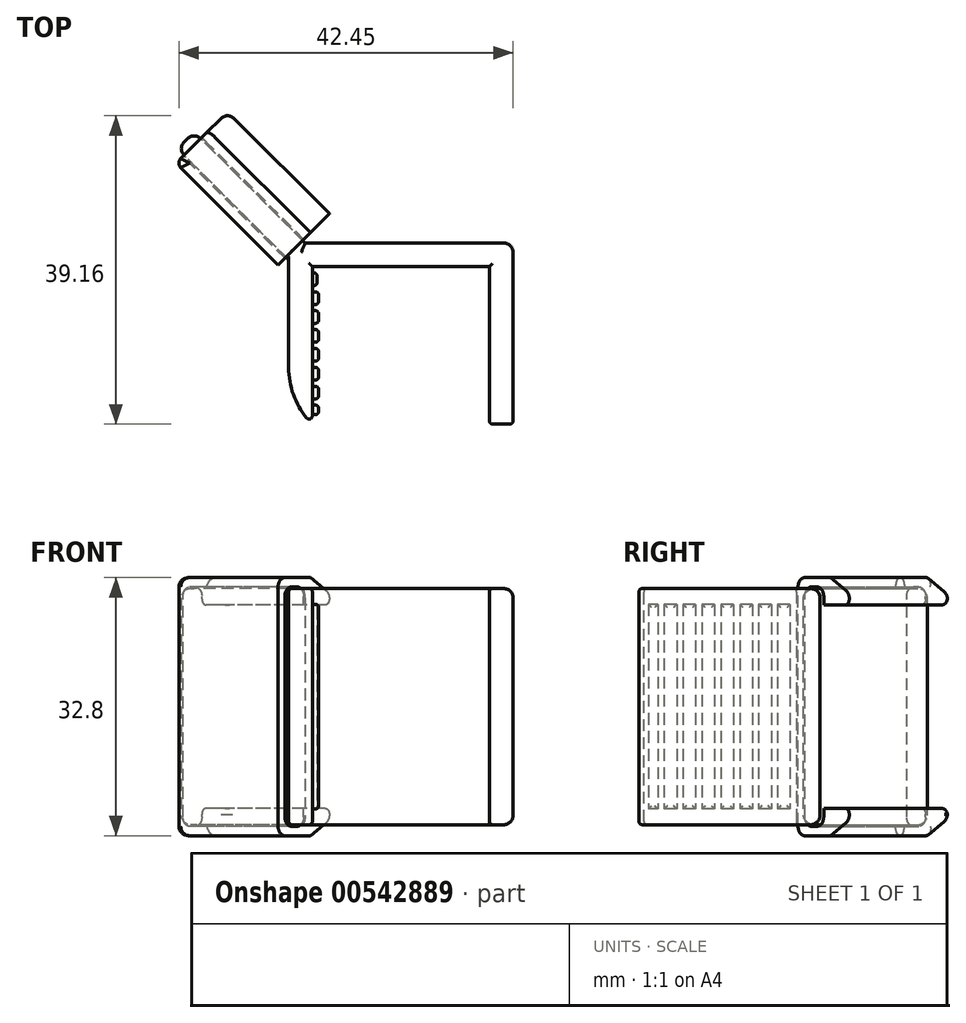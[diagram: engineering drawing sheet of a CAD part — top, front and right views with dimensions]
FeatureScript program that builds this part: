
annotation { "Feature Type Name" : "Feature", "Feature Type Description" : "" }
export const myFeature = defineFeature(function(context is Context, id is Id, definition is map)
    precondition{}
    {
        {
            var Q0;
            Q0=qCreatedBy(makeId("Top.planeOp"),FACE);
            var sketch = newSketch(context, id + "F0", { "sketchPlane" : qUnion([Q0])});
            skLineSegment(sketch, "E0", {"start": v(11.25, -14.71) * mm, "end": v(11.25, 5.29) * mm});
            skLineSegment(sketch, "E1", {"start": v(11.25, 5.29) * mm, "end": v(-11.25, 5.29) * mm});
            skLineSegment(sketch, "E2", {"start": v(-11.25, 5.29) * mm, "end": v(-11.25, -14.71) * mm});
            skLineSegment(sketch, "E3", {"start": v(-11.25, -14.71) * mm, "end": v(-14.25, -14.71) * mm});
            skLineSegment(sketch, "E4", {"start": v(-14.25, 8.29) * mm, "end": v(14.25, 8.29) * mm});
            skLineSegment(sketch, "E5", {"start": v(14.25, 8.29) * mm, "end": v(14.25, -14.71) * mm});
            skLineSegment(sketch, "E6", {"start": v(14.25, -14.71) * mm, "end": v(11.25, -14.71) * mm});
            skLineSegment(sketch, "E7", {"start": v(-14.25, 8.29) * mm, "end": v(-14.25, -14.71) * mm});
            skLineSegment(sketch, "E8.bottom", {"start": v(-14.25, 6.13) * mm, "end": v(-28.4, 20.28) * mm});
            skLineSegment(sketch, "E8.top", {"start": v(-12.13, 8.26) * mm, "end": v(-26.27, 22.4) * mm});
            skLineSegment(sketch, "E8.left", {"start": v(-14.25, 6.13) * mm, "end": v(-12.13, 8.26) * mm});
            skLineSegment(sketch, "E8.right", {"start": v(-28.4, 20.28) * mm, "end": v(-26.27, 22.4) * mm});
            skPoint(sketch, "E9", {"position": v(-10.45, 5.29) * mm});
            skLineSegment(sketch, "E10", {"start": v(-11.25, 4.49) * mm, "end": v(-10.65, 4.49) * mm});
            skLineSegment(sketch, "E11", {"start": v(-10.65, 4.49) * mm, "end": v(-10.65, 2.89) * mm});
            skLineSegment(sketch, "E12", {"start": v(-10.65, 2.89) * mm, "end": v(-11.25, 2.89) * mm});
            skPoint(sketch, "E13", {"position": v(0, 5.29) * mm});
            skLineSegment(sketch, "E14", {"start": v(-11.25, 2.09) * mm, "end": v(-10.45, 2.09) * mm});
            skLineSegment(sketch, "E15", {"start": v(-10.45, 2.09) * mm, "end": v(-10.45, 0.49) * mm});
            skLineSegment(sketch, "E16", {"start": v(-10.45, 0.49) * mm, "end": v(-11.25, 0.49) * mm});
            skLineSegment(sketch, "E17", {"start": v(-11.25, -0.31) * mm, "end": v(-10.45, -0.31) * mm});
            skLineSegment(sketch, "E18", {"start": v(-10.45, -0.31) * mm, "end": v(-10.45, -1.91) * mm});
            skLineSegment(sketch, "E19", {"start": v(-10.45, -1.91) * mm, "end": v(-11.25, -1.91) * mm});
            skLineSegment(sketch, "E20", {"start": v(-11.25, -2.71) * mm, "end": v(-10.45, -2.71) * mm});
            skLineSegment(sketch, "E21", {"start": v(-10.45, -2.71) * mm, "end": v(-10.45, -4.31) * mm});
            skLineSegment(sketch, "E22", {"start": v(-10.45, -4.31) * mm, "end": v(-11.25, -4.31) * mm});
            skLineSegment(sketch, "E23", {"start": v(-11.25, -5.11) * mm, "end": v(-10.45, -5.11) * mm});
            skLineSegment(sketch, "E24", {"start": v(-10.45, -5.11) * mm, "end": v(-10.45, -6.71) * mm});
            skLineSegment(sketch, "E25", {"start": v(-10.45, -6.71) * mm, "end": v(-11.25, -6.71) * mm});
            skLineSegment(sketch, "E26", {"start": v(-11.25, -7.51) * mm, "end": v(-10.45, -7.51) * mm});
            skLineSegment(sketch, "E27", {"start": v(-10.45, -7.51) * mm, "end": v(-10.45, -9.11) * mm});
            skLineSegment(sketch, "E28", {"start": v(-10.45, -9.11) * mm, "end": v(-11.25, -9.11) * mm});
            skLineSegment(sketch, "E29", {"start": v(-11.25, -9.91) * mm, "end": v(-10.45, -9.91) * mm});
            skLineSegment(sketch, "E30", {"start": v(-10.45, -9.91) * mm, "end": v(-10.45, -11.51) * mm});
            skLineSegment(sketch, "E31", {"start": v(-10.45, -11.51) * mm, "end": v(-11.25, -11.51) * mm});
            skLineSegment(sketch, "E32", {"start": v(-11.25, -12.31) * mm, "end": v(-10.45, -12.31) * mm});
            skLineSegment(sketch, "E33", {"start": v(-10.45, -12.31) * mm, "end": v(-10.45, -13.51) * mm});
            skLineSegment(sketch, "E34", {"start": v(-10.45, -13.51) * mm, "end": v(-11.25, -13.51) * mm});
            skSolve(sketch);
        }
        {
            var Q0;
            {var subQ4=sQuery(id+"F0.wireOp",EDGE,"E8.bottom");Q0=makeQuery(id+"F0.imprint","IMPRINT",FACE,{"disambiguationData":[TD([[makeQuery(id+"F0.imprint","IMPRINT",EDGE,{"derivedFrom":subQ4}),-1.0]])]});}
            var Q1;
            Q1=makeQuery(id+"F0.imprint","IMPRINT",FACE,{"disambiguationData":[TD([[makeQuery(id+"F0.imprint","IMPRINT",EDGE,{"derivedFrom":sQuery(id+"F0.wireOp",EDGE,"E0")}),-1.0]])]});
            var Q2;
            {var subQ5=sQuery(id+"F0.wireOp",EDGE,"E8.left");Q2=makeQuery(id+"F0.imprint","IMPRINT",FACE,{"disambiguationData":[TD([[makeQuery(id+"F0.imprint","IMPRINT",EDGE,{"derivedFrom":subQ5}),1.0]])]});}
            extrude(context, id + "F1", {"entities" : qUnion([Q0, Q1, Q2]), "depth" : 30 * mm});
        }
        {
            var Q0;
            Q0=makeQuery(id+"F1.opExtrude","SWEPT_EDGE",EDGE,{"disambiguationData":[OSD([sQuery(id+"F0.wireOp",EDGE,"E3"),sQuery(id+"F0.wireOp",EDGE,"E7")])]});
            fillet(context, id + "F2", {"entities" : qUnion([Q0]), "radius" : 10 * mm, "tangentPropagation" : true, "allowEdgeOverflow" : false});
        }
        {
            var Q0;
            Q0=makeQuery(id+"F1.opExtrude","SWEPT_EDGE",EDGE,{"disambiguationData":[OSD([sQuery(id+"F0.wireOp",EDGE,"E5"),sQuery(id+"F0.wireOp",EDGE,"E6")])]});
            var Q1;
            Q1=makeQuery(id+"F1.opExtrude","SWEPT_EDGE",EDGE,{"disambiguationData":[OSD([sQuery(id+"F0.wireOp",EDGE,"E0"),sQuery(id+"F0.wireOp",EDGE,"E6")])]});
            var Q2;
            Q2=makeQuery(id+"F2.opFillet","BLEND_EDGE",EDGE,{"blendedFrom":[makeQuery(id+"F1.opExtrude","SWEPT_EDGE",EDGE,{"disambiguationData":[OSD([sQuery(id+"F0.wireOp",EDGE,"E3"),sQuery(id+"F0.wireOp",EDGE,"E7")])]}),makeQuery(id+"F1.opExtrude","SWEPT_FACE",FACE,{"disambiguationData":[OSD([sQuery(id+"F0.wireOp",EDGE,"E2")])]})],"blendedInto":[makeQuery(id+"F1.opExtrude","SWEPT_FACE",FACE,{"disambiguationData":[OSD([sQuery(id+"F0.wireOp",EDGE,"E2")])]})]});
            var Q3;
            Q3=makeQuery(id+"F1.opExtrude","CAP_EDGE",EDGE,{"disambiguationData":[OSD([sQuery(id+"F0.wireOp",EDGE,"E2")])],"isStart":false});
            var Q4;
            Q4=makeQuery(id+"F1.opExtrude","CAP_EDGE",EDGE,{"disambiguationData":[OSD([sQuery(id+"F0.wireOp",EDGE,"E1")])],"isStart":false});
            var Q5;
            Q5=makeQuery(id+"F1.opExtrude","CAP_EDGE",EDGE,{"disambiguationData":[OSD([sQuery(id+"F0.wireOp",EDGE,"E0")])],"isStart":false});
            var Q6;
            Q6=makeQuery(id+"F1.opExtrude","CAP_EDGE",EDGE,{"disambiguationData":[OSD([sQuery(id+"F0.wireOp",EDGE,"E6")])],"isStart":false});
            var Q7;
            {var subQ0=sQuery(id+"F0.wireOp",EDGE,"E7");var subQ1=sQuery(id+"F0.wireOp",EDGE,"E3");Q7=makeQuery(id+"F2.opFillet","BLEND_EDGE",EDGE,{"blendedFrom":[makeQuery(id+"F1.opExtrude","SWEPT_EDGE",EDGE,{"disambiguationData":[OSD([subQ1,subQ0])]}),makeQuery(id+"F1.opExtrude","CAP_FACE",FACE,{"disambiguationData":[OSD([sQuery(id+"F0.wireOp",EDGE,"E0"),sQuery(id+"F0.wireOp",EDGE,"E1"),sQuery(id+"F0.wireOp",EDGE,"E2"),subQ1,sQuery(id+"F0.wireOp",EDGE,"E4"),sQuery(id+"F0.wireOp",EDGE,"E5"),sQuery(id+"F0.wireOp",EDGE,"E6"),subQ0,sQuery(id+"F0.wireOp",EDGE,"E8.bottom"),sQuery(id+"F0.wireOp",EDGE,"E8.top"),sQuery(id+"F0.wireOp",EDGE,"E8.right")])],"isStart":false})],"blendedInto":[makeQuery(id+"F1.opExtrude","CAP_FACE",FACE,{"disambiguationData":[OSD([sQuery(id+"F0.wireOp",EDGE,"E0"),sQuery(id+"F0.wireOp",EDGE,"E1"),sQuery(id+"F0.wireOp",EDGE,"E2"),subQ1,sQuery(id+"F0.wireOp",EDGE,"E4"),sQuery(id+"F0.wireOp",EDGE,"E5"),sQuery(id+"F0.wireOp",EDGE,"E6"),subQ0,sQuery(id+"F0.wireOp",EDGE,"E8.bottom"),sQuery(id+"F0.wireOp",EDGE,"E8.top"),sQuery(id+"F0.wireOp",EDGE,"E8.right")])],"isStart":false})]});}
            var Q8;
            {var subQ0=sQuery(id+"F0.wireOp",EDGE,"E7");var subQ1=sQuery(id+"F0.wireOp",EDGE,"E3");Q8=makeQuery(id+"F2.opFillet","BLEND_EDGE",EDGE,{"blendedFrom":[makeQuery(id+"F1.opExtrude","SWEPT_EDGE",EDGE,{"disambiguationData":[OSD([subQ1,subQ0])]}),makeQuery(id+"F1.opExtrude","CAP_FACE",FACE,{"disambiguationData":[OSD([sQuery(id+"F0.wireOp",EDGE,"E0"),sQuery(id+"F0.wireOp",EDGE,"E1"),sQuery(id+"F0.wireOp",EDGE,"E2"),subQ1,sQuery(id+"F0.wireOp",EDGE,"E4"),sQuery(id+"F0.wireOp",EDGE,"E5"),sQuery(id+"F0.wireOp",EDGE,"E6"),subQ0,sQuery(id+"F0.wireOp",EDGE,"E8.bottom"),sQuery(id+"F0.wireOp",EDGE,"E8.top"),sQuery(id+"F0.wireOp",EDGE,"E8.right")])],"isStart":true})],"blendedInto":[makeQuery(id+"F1.opExtrude","CAP_FACE",FACE,{"disambiguationData":[OSD([sQuery(id+"F0.wireOp",EDGE,"E0"),sQuery(id+"F0.wireOp",EDGE,"E1"),sQuery(id+"F0.wireOp",EDGE,"E2"),subQ1,sQuery(id+"F0.wireOp",EDGE,"E4"),sQuery(id+"F0.wireOp",EDGE,"E5"),sQuery(id+"F0.wireOp",EDGE,"E6"),subQ0,sQuery(id+"F0.wireOp",EDGE,"E8.bottom"),sQuery(id+"F0.wireOp",EDGE,"E8.top"),sQuery(id+"F0.wireOp",EDGE,"E8.right")])],"isStart":true})]});}
            var Q9;
            Q9=makeQuery(id+"F1.opExtrude","CAP_EDGE",EDGE,{"disambiguationData":[OSD([sQuery(id+"F0.wireOp",EDGE,"E2")])],"isStart":true});
            var Q10;
            Q10=makeQuery(id+"F1.opExtrude","CAP_EDGE",EDGE,{"disambiguationData":[OSD([sQuery(id+"F0.wireOp",EDGE,"E1")])],"isStart":true});
            var Q11;
            Q11=makeQuery(id+"F1.opExtrude","CAP_EDGE",EDGE,{"disambiguationData":[OSD([sQuery(id+"F0.wireOp",EDGE,"E0")])],"isStart":true});
            var Q12;
            Q12=makeQuery(id+"F1.opExtrude","CAP_EDGE",EDGE,{"disambiguationData":[OSD([sQuery(id+"F0.wireOp",EDGE,"E6")])],"isStart":true});
            fillet(context, id + "F3", {"entities" : qUnion([Q0, Q1, Q2, Q3, Q4, Q5, Q6, Q7, Q8, Q9, Q10, Q11, Q12]), "radius" : .4 * mm, "tangentPropagation" : true, "allowEdgeOverflow" : false});
        }
        {
            var Q0;
            Q0=makeQuery(id+"F1.opExtrude","SWEPT_EDGE",EDGE,{"disambiguationData":[OSD([sQuery(id+"F0.wireOp",EDGE,"E4"),sQuery(id+"F0.wireOp",EDGE,"E5")])]});
            var Q1;
            Q1=makeQuery(id+"F1.opExtrude","CAP_EDGE",EDGE,{"disambiguationData":[OSD([sQuery(id+"F0.wireOp",EDGE,"E5")])],"isStart":false});
            var Q2;
            Q2=makeQuery(id+"F1.opExtrude","CAP_EDGE",EDGE,{"disambiguationData":[OSD([sQuery(id+"F0.wireOp",EDGE,"E4")])],"isStart":false});
            var Q3;
            Q3=makeQuery(id+"F1.opExtrude","CAP_EDGE",EDGE,{"disambiguationData":[OSD([sQuery(id+"F0.wireOp",EDGE,"E5")])],"isStart":true});
            var Q4;
            Q4=makeQuery(id+"F1.opExtrude","CAP_EDGE",EDGE,{"disambiguationData":[OSD([sQuery(id+"F0.wireOp",EDGE,"E4")])],"isStart":true});
            var Q5;
            Q5=makeQuery(id+"F1.opExtrude","CAP_EDGE",EDGE,{"disambiguationData":[OSD([sQuery(id+"F0.wireOp",EDGE,"E8.top")])],"isStart":false});
            var Q6;
            Q6=makeQuery(id+"F1.opExtrude","SWEPT_EDGE",EDGE,{"disambiguationData":[OSD([sQuery(id+"F0.wireOp",EDGE,"E8.top"),sQuery(id+"F0.wireOp",EDGE,"E8.right")])]});
            var Q7;
            Q7=makeQuery(id+"F1.opExtrude","SWEPT_EDGE",EDGE,{"disambiguationData":[OSD([sQuery(id+"F0.wireOp",EDGE,"E8.bottom"),sQuery(id+"F0.wireOp",EDGE,"E8.right")])]});
            var Q8;
            Q8=makeQuery(id+"F1.opExtrude","CAP_EDGE",EDGE,{"disambiguationData":[OSD([sQuery(id+"F0.wireOp",EDGE,"E8.bottom")])],"isStart":false});
            var Q9;
            Q9=makeQuery(id+"F1.opExtrude","CAP_EDGE",EDGE,{"disambiguationData":[OSD([sQuery(id+"F0.wireOp",EDGE,"E8.right")])],"isStart":false});
            var Q10;
            Q10=makeQuery(id+"F1.opExtrude","CAP_EDGE",EDGE,{"disambiguationData":[OSD([sQuery(id+"F0.wireOp",EDGE,"E8.right")])],"isStart":true});
            var Q11;
            Q11=makeQuery(id+"F1.opExtrude","CAP_EDGE",EDGE,{"disambiguationData":[OSD([sQuery(id+"F0.wireOp",EDGE,"E8.top")])],"isStart":true});
            var Q12;
            Q12=makeQuery(id+"F1.opExtrude","CAP_EDGE",EDGE,{"disambiguationData":[OSD([sQuery(id+"F0.wireOp",EDGE,"E8.bottom")])],"isStart":true});
            fillet(context, id + "F4", {"entities" : qUnion([Q0, Q1, Q2, Q3, Q4, Q5, Q6, Q7, Q8, Q9, Q10, Q11, Q12]), "radius" : 1.2 * mm, "tangentPropagation" : true, "allowEdgeOverflow" : false});
        }
        {
            var Q0;
            {var subQ0=sQuery(id+"F0.wireOp",EDGE,"E10");Q0=makeQuery(id+"F0.imprint","IMPRINT",FACE,{"disambiguationData":[TD([[makeQuery(id+"F0.imprint","IMPRINT",EDGE,{"derivedFrom":subQ0}),-1.0]])]});}
            var Q1;
            {var subQ0=sQuery(id+"F0.wireOp",EDGE,"E14");Q1=makeQuery(id+"F0.imprint","IMPRINT",FACE,{"disambiguationData":[TD([[makeQuery(id+"F0.imprint","IMPRINT",EDGE,{"derivedFrom":subQ0}),-1.0]])]});}
            var Q2;
            {var subQ0=sQuery(id+"F0.wireOp",EDGE,"E17");Q2=makeQuery(id+"F0.imprint","IMPRINT",FACE,{"disambiguationData":[TD([[makeQuery(id+"F0.imprint","IMPRINT",EDGE,{"derivedFrom":subQ0}),-1.0]])]});}
            var Q3;
            {var subQ0=sQuery(id+"F0.wireOp",EDGE,"E20");Q3=makeQuery(id+"F0.imprint","IMPRINT",FACE,{"disambiguationData":[TD([[makeQuery(id+"F0.imprint","IMPRINT",EDGE,{"derivedFrom":subQ0}),-1.0]])]});}
            var Q4;
            {var subQ0=sQuery(id+"F0.wireOp",EDGE,"E23");Q4=makeQuery(id+"F0.imprint","IMPRINT",FACE,{"disambiguationData":[TD([[makeQuery(id+"F0.imprint","IMPRINT",EDGE,{"derivedFrom":subQ0}),-1.0]])]});}
            var Q5;
            {var subQ0=sQuery(id+"F0.wireOp",EDGE,"E26");Q5=makeQuery(id+"F0.imprint","IMPRINT",FACE,{"disambiguationData":[TD([[makeQuery(id+"F0.imprint","IMPRINT",EDGE,{"derivedFrom":subQ0}),-1.0]])]});}
            var Q6;
            {var subQ0=sQuery(id+"F0.wireOp",EDGE,"E29");Q6=makeQuery(id+"F0.imprint","IMPRINT",FACE,{"disambiguationData":[TD([[makeQuery(id+"F0.imprint","IMPRINT",EDGE,{"derivedFrom":subQ0}),-1.0]])]});}
            var Q7;
            {var subQ0=sQuery(id+"F0.wireOp",EDGE,"E32");Q7=makeQuery(id+"F0.imprint","IMPRINT",FACE,{"disambiguationData":[TD([[makeQuery(id+"F0.imprint","IMPRINT",EDGE,{"derivedFrom":subQ0}),-1.0]])]});}
            extrude(context, id + "F5", {"entities" : qUnion([Q0, Q1, Q2, Q3, Q4, Q5, Q6, Q7]), "operationType" : NewBodyOperationType.ADD, "depth" : 28 * mm, "hasSecondDirection" : true, "secondDirectionOppositeDirection" : false, "secondDirectionDepth" : 2 * mm});
        }
        {
            var Q0;
            Q0=makeQuery(id+"F5.opExtrude","SWEPT_EDGE",EDGE,{"disambiguationData":[OSD([sQuery(id+"F0.wireOp",EDGE,"E10"),sQuery(id+"F0.wireOp",EDGE,"E11")])]});
            var Q1;
            Q1=makeQuery(id+"F5.opExtrude","SWEPT_FACE",FACE,{"disambiguationData":[OSD([sQuery(id+"F0.wireOp",EDGE,"E11")])]});
            var Q2;
            Q2=makeQuery(id+"F5.opExtrude","SWEPT_FACE",FACE,{"disambiguationData":[OSD([sQuery(id+"F0.wireOp",EDGE,"E15")])]});
            var Q3;
            Q3=makeQuery(id+"F5.opExtrude","SWEPT_FACE",FACE,{"disambiguationData":[OSD([sQuery(id+"F0.wireOp",EDGE,"E18")])]});
            var Q4;
            Q4=makeQuery(id+"F5.opExtrude","SWEPT_FACE",FACE,{"disambiguationData":[OSD([sQuery(id+"F0.wireOp",EDGE,"E21")])]});
            var Q5;
            Q5=makeQuery(id+"F5.opExtrude","SWEPT_FACE",FACE,{"disambiguationData":[OSD([sQuery(id+"F0.wireOp",EDGE,"E24")])]});
            var Q6;
            Q6=makeQuery(id+"F5.opExtrude","SWEPT_FACE",FACE,{"disambiguationData":[OSD([sQuery(id+"F0.wireOp",EDGE,"E27")])]});
            var Q7;
            Q7=makeQuery(id+"F5.opExtrude","SWEPT_FACE",FACE,{"disambiguationData":[OSD([sQuery(id+"F0.wireOp",EDGE,"E30")])]});
            var Q8;
            Q8=makeQuery(id+"F5.opExtrude","SWEPT_FACE",FACE,{"disambiguationData":[OSD([sQuery(id+"F0.wireOp",EDGE,"E33")])]});
            fillet(context, id + "F6", {"entities" : qUnion([Q0, Q1, Q2, Q3, Q4, Q5, Q6, Q7, Q8]), "radius" : .4 * mm, "tangentPropagation" : true, "allowEdgeOverflow" : false});
        }
        {
            var Q0;
            Q0=makeQuery(id+"F1.opExtrude","SWEPT_FACE",FACE,{"disambiguationData":[OSD([sQuery(id+"F0.wireOp",EDGE,"E8.right")])]});
            var sketch = newSketch(context, id + "F7", { "sketchPlane" : qUnion([Q0])});
            skPoint(sketch, "E35", {"position": v(4.24, 15) * mm});
            skPoint(sketch, "E35.positionSnap0", {"position": v(4.24, 30) * mm});
            skPoint(sketch, "E35.positionSnap1", {"position": v(5.94, 15) * mm});
            skLineSegment(sketch, "E36.bottom", {"start": v(2.54, -0.2) * mm, "end": v(5.94, -0.2) * mm});
            skLineSegment(sketch, "E36.top", {"start": v(2.54, 30.2) * mm, "end": v(5.94, 30.2) * mm});
            skLineSegment(sketch, "E36.left", {"start": v(2.54, -0.2) * mm, "end": v(2.54, 2.1) * mm});
            skLineSegment(sketch, "E36.right", {"start": v(5.94, -0.2) * mm, "end": v(5.94, 30.2) * mm});
            skLineSegment(sketch, "E37.bottom", {"start": v(1.34, -1.4) * mm, "end": v(7.14, -1.4) * mm});
            skLineSegment(sketch, "E37.top", {"start": v(1.34, 31.4) * mm, "end": v(7.14, 31.4) * mm});
            skLineSegment(sketch, "E37.right", {"start": v(7.14, -1.4) * mm, "end": v(7.14, 31.4) * mm});
            skLineSegment(sketch, "E38", {"start": v(1.34, -1.4) * mm, "end": v(-2.06, 0.6) * mm});
            skLineSegment(sketch, "E39", {"start": v(-2.06, 0.6) * mm, "end": v(-2.06, 2.1) * mm});
            skLineSegment(sketch, "E40", {"start": v(-2.06, 2.1) * mm, "end": v(2.54, 2.1) * mm});
            skLineSegment(sketch, "E41", {"start": v(1.34, 31.4) * mm, "end": v(-2.06, 29.4) * mm});
            skLineSegment(sketch, "E42", {"start": v(-2.06, 29.4) * mm, "end": v(-2.06, 27.9) * mm});
            skLineSegment(sketch, "E43", {"start": v(-2.06, 27.9) * mm, "end": v(2.54, 27.9) * mm});
            skLineSegment(sketch, "E44.trimOffspring", {"start": v(2.54, 27.9) * mm, "end": v(2.54, 30.2) * mm});
            skPoint(sketch, "E45", {"position": v(4.24, -0.2) * mm});
            skPoint(sketch, "E46", {"position": v(7.14, 15) * mm});
            skSolve(sketch);
        }
        {
            var Q0;
            Q0=makeQuery(id+"F7.imprint","IMPRINT",FACE,{"disambiguationData":[TD([[makeQuery(id+"F7.imprint","IMPRINT",EDGE,{"derivedFrom":sQuery(id+"F7.wireOp",EDGE,"E36.bottom")}),-1.0]])]});
            extrude(context, id + "F8", {"entities" : qUnion([Q0]), "oppositeDirection" : true, "depth" : 19.5 * mm, "hasSecondDirection" : true, "secondDirectionOppositeDirection" : true, "secondDirectionDepth" : 1.2 * mm});
        }
        {
            var Q0;
            Q0=makeQuery(id+"F8.opExtrude","SWEPT_EDGE",EDGE,{"disambiguationData":[OSD([sQuery(id+"F7.wireOp",EDGE,"E37.bottom"),sQuery(id+"F7.wireOp",EDGE,"E37.right")])]});
            var Q1;
            Q1=makeQuery(id+"F8.opExtrude","SWEPT_EDGE",EDGE,{"disambiguationData":[OSD([sQuery(id+"F7.wireOp",EDGE,"E37.top"),sQuery(id+"F7.wireOp",EDGE,"E37.right")])]});
            var Q2;
            Q2=makeQuery(id+"F8.opExtrude","SWEPT_EDGE",EDGE,{"disambiguationData":[OSD([sQuery(id+"F7.wireOp",EDGE,"E41"),sQuery(id+"F7.wireOp",EDGE,"E42")])]});
            var Q3;
            Q3=makeQuery(id+"F8.opExtrude","SWEPT_EDGE",EDGE,{"disambiguationData":[OSD([sQuery(id+"F7.wireOp",EDGE,"E38"),sQuery(id+"F7.wireOp",EDGE,"E39")])]});
            var Q4;
            Q4=makeQuery(id+"F8.opExtrude","CAP_EDGE",EDGE,{"disambiguationData":[OSD([sQuery(id+"F7.wireOp",EDGE,"E42")])],"isStart":true});
            var Q5;
            Q5=makeQuery(id+"F8.opExtrude","CAP_EDGE",EDGE,{"disambiguationData":[OSD([sQuery(id+"F7.wireOp",EDGE,"E37.top")])],"isStart":true});
            var Q6;
            Q6=makeQuery(id+"F8.opExtrude","CAP_EDGE",EDGE,{"disambiguationData":[OSD([sQuery(id+"F7.wireOp",EDGE,"E39")])],"isStart":true});
            var Q7;
            Q7=makeQuery(id+"F8.opExtrude","CAP_EDGE",EDGE,{"disambiguationData":[OSD([sQuery(id+"F7.wireOp",EDGE,"E37.bottom")])],"isStart":true});
            var Q8;
            Q8=makeQuery(id+"F8.opExtrude","CAP_EDGE",EDGE,{"disambiguationData":[OSD([sQuery(id+"F7.wireOp",EDGE,"E38")])],"isStart":true});
            var Q9;
            Q9=makeQuery(id+"F8.opExtrude","CAP_EDGE",EDGE,{"disambiguationData":[OSD([sQuery(id+"F7.wireOp",EDGE,"E41")])],"isStart":true});
            fillet(context, id + "F9", {"entities" : qUnion([Q0, Q1, Q2, Q3, Q4, Q5, Q6, Q7, Q8, Q9]), "radius" : 1.2 * mm, "tangentPropagation" : true, "allowEdgeOverflow" : false});
        }
        {
            var Q0;
            Q0=makeQuery(id+"F8.opExtrude","SWEPT_EDGE",EDGE,{"disambiguationData":[OSD([sQuery(id+"F7.wireOp",EDGE,"E36.top"),sQuery(id+"F7.wireOp",EDGE,"E44.trimOffspring")])]});
            var Q1;
            Q1=makeQuery(id+"F8.opExtrude","SWEPT_EDGE",EDGE,{"disambiguationData":[OSD([sQuery(id+"F7.wireOp",EDGE,"E36.top"),sQuery(id+"F7.wireOp",EDGE,"E36.right")])]});
            var Q2;
            Q2=makeQuery(id+"F8.opExtrude","SWEPT_EDGE",EDGE,{"disambiguationData":[OSD([sQuery(id+"F7.wireOp",EDGE,"E36.bottom"),sQuery(id+"F7.wireOp",EDGE,"E36.right")])]});
            var Q3;
            Q3=makeQuery(id+"F8.opExtrude","SWEPT_EDGE",EDGE,{"disambiguationData":[OSD([sQuery(id+"F7.wireOp",EDGE,"E36.bottom"),sQuery(id+"F7.wireOp",EDGE,"E36.left")])]});
            fillet(context, id + "F10", {"entities" : qUnion([Q0, Q1, Q2, Q3]), "radius" : 1.2 * mm, "tangentPropagation" : true, "allowEdgeOverflow" : false});
        }
        {
            var Q0;
            Q0=makeQuery(id+"F8.opExtrude","CAP_EDGE",EDGE,{"disambiguationData":[OSD([sQuery(id+"F7.wireOp",EDGE,"E37.right")])],"isStart":true});
            var Q1;
            Q1=makeQuery(id+"F8.opExtrude","SWEPT_EDGE",EDGE,{"disambiguationData":[OSD([sQuery(id+"F7.wireOp",EDGE,"E39"),sQuery(id+"F7.wireOp",EDGE,"E40")])]});
            var Q2;
            Q2=makeQuery(id+"F8.opExtrude","SWEPT_EDGE",EDGE,{"disambiguationData":[OSD([sQuery(id+"F7.wireOp",EDGE,"E42"),sQuery(id+"F7.wireOp",EDGE,"E43")])]});
            fillet(context, id + "F11", {"entities" : qUnion([Q0, Q1, Q2]), "radius" : .8 * mm, "tangentPropagation" : true, "allowEdgeOverflow" : false});
        }
    });
